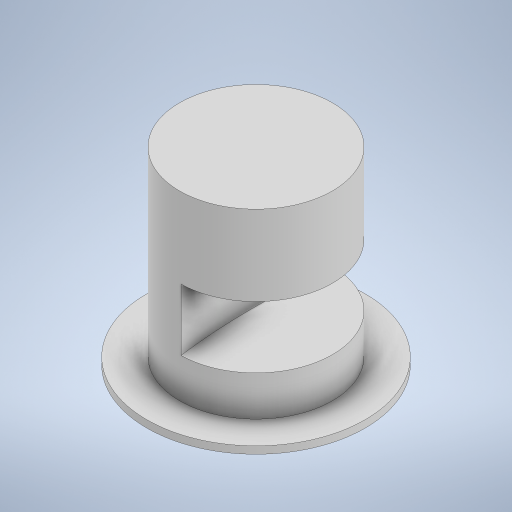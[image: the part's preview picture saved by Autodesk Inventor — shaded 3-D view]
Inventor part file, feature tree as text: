
AUTODESK INVENTOR PART (.ipt)
format: ipt  version: 2024.1 (Build 281209000, 209)  size: 254,976 bytes
history: native  units: mm
features: extrude x4, sketch x4, other x2
ambient origin geometry x8: Origin, YZ Plane, XZ Plane, XY Plane, X Axis, Y Axis, Z Axis, Center Point
bodies: Body1 (feature_tree)
feature tree (10):
  other  "ソリッド1"
  extrude  "押し出し1"  Depth=30.0mm
  extrude  "押し出し2"  Depth=1.0mm TaperAngle=0.0deg
  other  "作業平面1"
  extrude  "押し出し3"  Depth=21.0mm
  extrude  "押し出し4"  Depth=25.0mm TaperAngle=0.0deg
  sketch  "スケッチ1"
  sketch  "スケッチ2"
  sketch  "スケッチ4"
  sketch  "スケッチ5"
